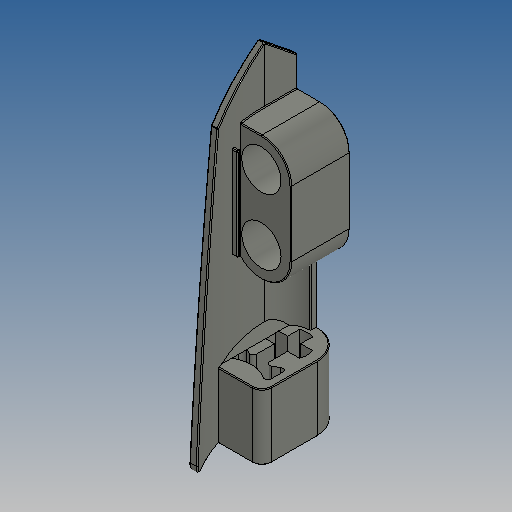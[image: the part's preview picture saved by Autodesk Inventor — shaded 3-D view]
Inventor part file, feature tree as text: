
AUTODESK INVENTOR PART (.ipt)
format: ipt  version: 2025 (Build 290162010, 162A)  size: 523,776 bytes
history: native  units: in
note: dims shown in document units (in); Inventor stores cm internally (conversion verified against a paired STEP export)
features: extrude x12, sketch x4, plane x1, fillet x1
ambient origin geometry x8: Origin, YZ Plane, XZ Plane, XY Plane, X Axis, Y Axis, Z Axis, Center Point
bodies: Solid1 (feature_tree)
feature tree (18):
  sketch  "Sketch2"  dims[d3=0.315in d4=0.0in d5=0.0315in]
  extrude  "Extrusion1"  Depth=0.315in
  sketch  "Sketch3"  dims[d16=0.4724in d17=0.0in d33=0.0157in d34=0.0in]
  extrude  "Extrusion4"  Depth=0.0157in TaperAngle=0.0deg
  extrude  "Extrusion8"  Depth=0.315in
  extrude  "Extrusion7"  Depth=0.1575in
  extrude  "Extrusion29"  Depth=0.1575in
  extrude  "Extrusion30"  Depth=0.1575in
  extrude  "Extrusion23"  Depth=0.1575in
  extrude  "Extrusion24"  Depth=0.1575in
  extrude  "Extrusion25"  Depth=0.0039in
  extrude  "Extrusion26"  Depth=0.1575in TaperAngle=0.0deg
  extrude  "Extrusion27"  Depth=0.1575in TaperAngle=0.0deg
  plane  "Work Plane2"
  extrude  "Extrusion28"  Depth=0.1575in TaperAngle=0.0deg
  fillet  "Fillet2"  Radius=0.0315in
  sketch  "Sketch5"  dims[d37=0.7244in d38=0.0in d45=0.378in d46=0.315in]
  sketch  "Sketch12"  dims[d85=0.315in d86=0.252in d87=0.189in d88=0.2835in d89=0.0394in d90=0.7874in d91=0.0039in d92=0.2835in d93=0.0in d94=0.2835in d95=0.0in d96=0.2835in d97=0.0in d98=0.0315in d99=0.0in d100=0.252in d101=0.0in d102=0.0327in d103=0.0157in d104=0.0315in d105=0.4409in d106=0.0in d108=0.0039in d109=0.0157in d110=0.189in d111=0.2835in d112=0.0354in d113=0.315in d114=0.063in d115=0.0157in d116=0.3937in d117=0.0in d118=0.3937in d119=0.0in d120=0.8661in d121=0.242in d122=0.0472in d123=0.2008in d124=1.3071in d125=1.3858in d126=0.1575in d127=0.4252in d128=0.0394in]
